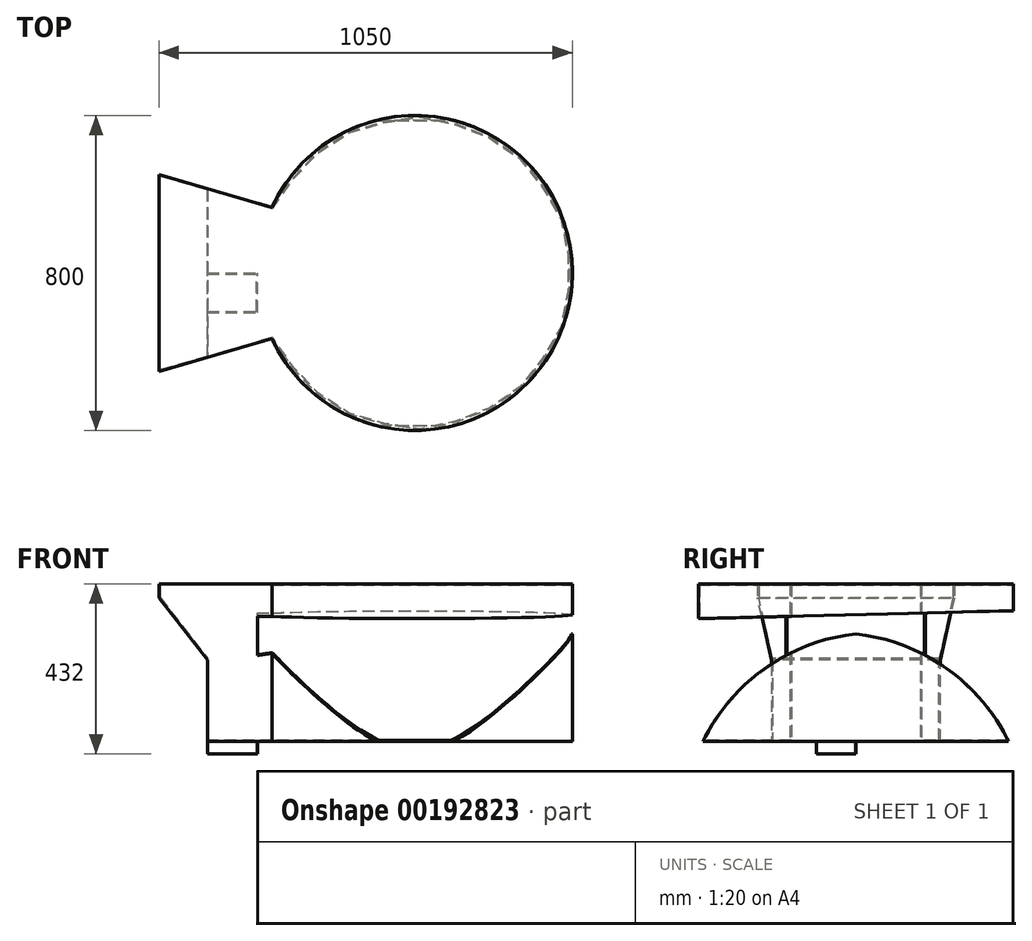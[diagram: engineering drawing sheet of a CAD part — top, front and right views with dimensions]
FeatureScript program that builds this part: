
annotation { "Feature Type Name" : "Feature", "Feature Type Description" : "" }
export const myFeature = defineFeature(function(context is Context, id is Id, definition is map)
    precondition{}
    {
        {
            var Q0;
            Q0=qCreatedBy(makeId("Front.planeOp"),FACE);
            var sketch = newSketch(context, id + "F0", { "sketchPlane" : qUnion([Q0])});
            skArc(sketch, "E0", {"start": v(-400, 0) * mm, "mid": v(-384.82, 109.14) * mm, "end": v(-340.44, 210) * mm, "construction": true});
            skLineSegment(sketch, "E1", {"start": v(-340.44, 210) * mm, "end": v(-650, 210) * mm, "construction": true});
            skLineSegment(sketch, "E2", {"start": v(-650, 210) * mm, "end": v(-650, 0) * mm, "construction": true});
            skLineSegment(sketch, "E3", {"start": v(-650, 0) * mm, "end": v(-400, 0) * mm});
            skLineSegment(sketch, "E4.left", {"start": v(-400, 0) * mm, "end": v(-400, 32) * mm});
            skLineSegment(sketch, "E5", {"start": v(-650, 32) * mm, "end": v(-400, 32) * mm});
            skArc(sketch, "E6", {"start": v(340.44, 210) * mm, "mid": v(0, 308.06) * mm, "end": v(-340.44, 210) * mm, "construction": true});
            skArc(sketch, "E7.trimOffspring", {"start": v(340.44, 210) * mm, "mid": v(384.82, 109.14) * mm, "end": v(400, 0) * mm, "construction": true});
            skPoint(sketch, "E8.MirrorCS.end.orphan", {"position": v(650, 210) * mm});
            skLineSegment(sketch, "E9", {"start": v(-650, 32) * mm, "end": v(-650, 0) * mm});
            skSolve(sketch);
        }
        {
            var Q0;
            Q0=makeQuery(id+"F0.imprint","IMPRINT",FACE,{"disambiguationData":[TD([[makeQuery(id+"F0.imprint","IMPRINT",EDGE,{"derivedFrom":sQuery(id+"F0.wireOp",EDGE,"E3")}),1.0]])]});
            extrude(context, id + "F1", {"entities" : qUnion([Q0]), "depth" : 100 * mm});
        }
        {
            var Q0;
            Q0=makeQuery(id+"F1.opExtrude","SWEPT_FACE",FACE,{"disambiguationData":[OSD([sQuery(id+"F0.wireOp",EDGE,"E5")])]});
            var sketch = newSketch(context, id + "F2", { "sketchPlane" : qUnion([Q0])});
            skLineSegment(sketch, "E10", {"start": v(-650, 250) * mm, "end": v(-650, -250) * mm});
            skLineSegment(sketch, "E11", {"start": v(-650, -250) * mm, "end": v(-340.44, -160) * mm});
            skLineSegment(sketch, "E12", {"start": v(-340.44, -160) * mm, "end": v(-340.44, 160) * mm});
            skLineSegment(sketch, "E13", {"start": v(-340.44, 160) * mm, "end": v(-650, 250) * mm});
            skArc(sketch, "E14", {"start": v(-363.6, -166.73) * mm, "mid": v(400, 0) * mm, "end": v(-363.6, 166.73) * mm});
            skSolve(sketch);
        }
        {
            var Q0;
            {var subQ0=sQuery(id+"F2.wireOp",EDGE,"E12");Q0=makeQuery(id+"F2.imprint","IMPRINT",FACE,{"disambiguationData":[TD([[makeQuery(id+"F2.imprint","IMPRINT",EDGE,{"derivedFrom":subQ0}),-1.0]])]});}
            var Q1;
            {var subQ0=sQuery(id+"F2.wireOp",EDGE,"E12");Q1=makeQuery(id+"F2.imprint","IMPRINT",FACE,{"disambiguationData":[TD([[makeQuery(id+"F2.imprint","IMPRINT",EDGE,{"derivedFrom":subQ0}),1.0]])]});}
            var Q2;
            {var subQ1=sQuery(id+"F0.wireOp",EDGE,"E5");var subQ2=makeQuery(id+"F1.opExtrude","CAP_EDGE",EDGE,{"disambiguationData":[OSD([subQ1])],"isStart":true});Q2=makeQuery(id+"F2.imprint","IMPRINT",FACE,{"disambiguationData":[TD([[makeQuery(id+"F2.imprint","IMPRINT",EDGE,{"derivedFrom":subQ2}),-1.0]])]});}
            extrude(context, id + "F3", {"entities" : qUnion([Q0, Q1, Q2]), "operationType" : NewBodyOperationType.ADD, "depth" : 400 * mm});
        }
        {
            var Q0;
            Q0=qCreatedBy(makeId("Front.planeOp"),FACE);
            var sketch = newSketch(context, id + "F4", { "sketchPlane" : qUnion([Q0])});
            skArc(sketch, "E15.0", {"start": v(340.44, 210) * mm, "mid": v(384.82, 109.14) * mm, "end": v(400, 0) * mm});
            skArc(sketch, "E15.1", {"start": v(340.44, 210) * mm, "mid": v(0, 308.06) * mm, "end": v(-340.44, 210) * mm});
            skArc(sketch, "E15.2", {"start": v(-400, 0) * mm, "mid": v(-384.82, 109.14) * mm, "end": v(-340.44, 210) * mm});
            skLineSegment(sketch, "E15.3", {"start": v(-340.44, 210) * mm, "end": v(-650, 210) * mm});
            skLineSegment(sketch, "E16", {"start": v(-340.44, 210) * mm, "end": v(-527.43, 239.12) * mm});
            skLineSegment(sketch, "E17", {"start": v(-527.43, 0) * mm, "end": v(-527.43, 239.12) * mm});
            skLineSegment(sketch, "E18", {"start": v(400, 0) * mm, "end": v(508.44, 0) * mm});
            skLineSegment(sketch, "E19", {"start": v(508.44, 0) * mm, "end": v(460.22, 508.48) * mm});
            skLineSegment(sketch, "E20", {"start": v(460.22, 508.48) * mm, "end": v(-737.07, 508.48) * mm});
            skLineSegment(sketch, "E21", {"start": v(-737.07, 508.48) * mm, "end": v(-527.43, 239.12) * mm});
            skLineSegment(sketch, "E22", {"start": v(-527.43, 0) * mm, "end": v(-527.43, -75.58) * mm});
            skLineSegment(sketch, "E23", {"start": v(-527.43, -75.58) * mm, "end": v(-737.07, -75.58) * mm});
            skLineSegment(sketch, "E24", {"start": v(-737.07, -75.58) * mm, "end": v(-737.07, 508.48) * mm});
            skSolve(sketch);
        }
        {
            var Q0;
            Q0=makeQuery(id+"F4.imprint","IMPRINT",FACE,{"disambiguationData":[TD([[makeQuery(id+"F4.imprint","IMPRINT",EDGE,{"derivedFrom":sQuery(id+"F4.wireOp",EDGE,"E15.0")}),1.0]])]});
            var Q1;
            {var subQ1=sQuery(id+"F4.wireOp",EDGE,"E21");Q1=makeQuery(id+"F4.imprint","IMPRINT",FACE,{"disambiguationData":[TD([[makeQuery(id+"F4.imprint","IMPRINT",EDGE,{"derivedFrom":subQ1}),-1.0]])]});}
            extrude(context, id + "F5", {"entities" : qUnion([Q0, Q1]), "operationType" : NewBodyOperationType.REMOVE, "endBound" : BoundingType.SYMMETRIC, "oppositeDirection" : true, "depth" : 800 * mm});
        }
        {
            var Q0;
            Q0=makeQuery(id+"F5.boolean.opBoolean","COPY",FACE,{"derivedFrom":makeQuery(id+"F5.opExtrude","SWEPT_FACE",FACE,{"disambiguationData":[OSD([sQuery(id+"F4.wireOp",EDGE,"E17"),sQuery(id+"F4.wireOp",EDGE,"E22")])]})});
            shell(context, id + "F6", {"entities" : qUnion([Q0]), "thickness" : 2.5 * mm});
        }
        {
            var Q0;
            Q0=qCreatedBy(makeId("Right.planeOp"),FACE);
            var sketch = newSketch(context, id + "F7", { "sketchPlane" : qUnion([Q0])});
            skArc(sketch, "E25", {"start": v(402.34, 0) * mm, "mid": v(243.27, 208.06) * mm, "end": v(0, 305.06) * mm});
            skArc(sketch, "E26.MirrorCS", {"start": v(-402.34, 0) * mm, "mid": v(-243.27, 208.06) * mm, "end": v(0, 305.06) * mm});
            skLineSegment(sketch, "E27", {"start": v(-402.34, 0) * mm, "end": v(-514.82, 340.9) * mm});
            skLineSegment(sketch, "E28", {"start": v(-514.82, 340.9) * mm, "end": v(523.47, 366.86) * mm});
            skLineSegment(sketch, "E29", {"start": v(523.47, 366.86) * mm, "end": v(402.34, 0) * mm});
            skSolve(sketch);
        }
        {
            var Q0;
            Q0=makeQuery(id+"F7.imprint","IMPRINT",FACE,{"disambiguationData":[TD([[makeQuery(id+"F7.imprint","IMPRINT",EDGE,{"derivedFrom":sQuery(id+"F7.wireOp",EDGE,"E25")}),-1.0]])]});
            extrude(context, id + "F8", {"entities" : qUnion([Q0]), "operationType" : NewBodyOperationType.REMOVE, "endBound" : BoundingType.SYMMETRIC, "oppositeDirection" : true, "depth" : 800 * mm});
        }
    });
